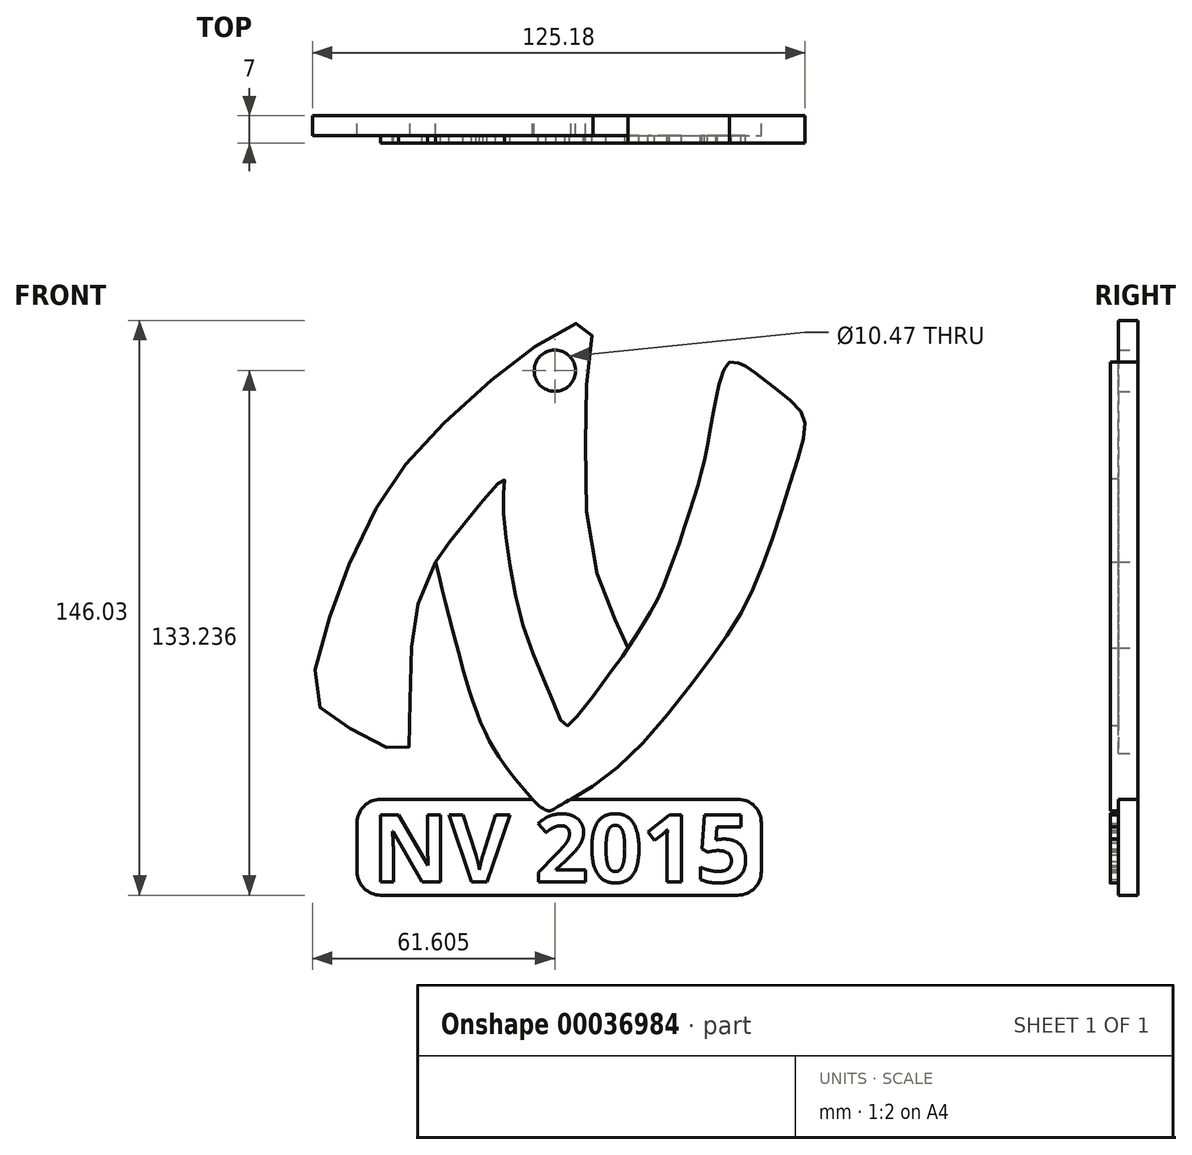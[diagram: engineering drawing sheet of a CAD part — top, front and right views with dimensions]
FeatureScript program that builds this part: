
annotation { "Feature Type Name" : "Feature", "Feature Type Description" : "" }
export const myFeature = defineFeature(function(context is Context, id is Id, definition is map)
    precondition{}
    {
        {
            var Q0;
            Q0=qCreatedBy(makeId("Front.planeOp"),FACE);
            var sketch = newSketch(context, id + "F0", { "sketchPlane" : qUnion([Q0])});
            skFitSpline(sketch, "E0", {"points": [v(-62.05, 9.72) * mm, v(-68.35, 7.94) * mm, v(-78.4, 1.78) * mm, v(-91.86, -9.18) * mm, v(-106.01, -23.1) * mm, v(-113.77, -33.15) * mm, v(-122.67, -50.27) * mm, v(-128.38, -65.56) * mm, v(-132.3, -79.85) * mm, v(-131.8, -87.25) * mm, v(-125.41, -92.27) * mm, v(-121.53, -94.78) * mm, v(-112.63, -99.12) * mm, v(-108.98, -100) * mm, v(-108.07, -97.06) * mm, v(-107.96, -84.07) * mm, v(-107.38, -70.36) * mm, v(-105.68, -61.25) * mm, v(-101.45, -51.4) * mm, v(-90.49, -37.26) * mm, v(-84.1, -30.4) * mm, v(-84.1, -33.38) * mm, v(-83.41, -46.84) * mm, v(-78.16, -70.81) * mm, v(-71.09, -88.16) * mm, v(-68.35, -93.18) * mm, v(-65.32, -90.4) * mm, v(-62.57, -87.07) * mm, v(-59.09, -82.37) * mm, v(-54.2, -75.83) * mm, v(-52.6, -73.32) * mm, v(-53.97, -70.36) * mm, v(-57.16, -62.82) * mm, v(-61.95, -48.67) * mm, v(-63.32, -25.61) * mm, v(-63.1, -7.12) * mm, v(-61.73, 5.66) * mm, v(-62.05, 9.72) * mm]});
            skFitSpline(sketch, "E1", {"points": [v(-26.83, -0.71) * mm, v(-24.57, -0.87) * mm, v(-23.23, -1.48) * mm, v(-21.78, -2.33) * mm, v(-13.33, -8.72) * mm, v(-8.31, -13.74) * mm, v(-7.63, -17.62) * mm, v(-10.3, -28) * mm, v(-16.53, -47.3) * mm, v(-23.38, -63.5) * mm, v(-35.48, -81.31) * mm, v(-57.16, -105.28) * mm, v(-70.17, -113.5) * mm, v(-73.14, -114.64) * mm, v(-78.85, -109.39) * mm, v(-87.06, -98.2) * mm, v(-93.91, -80.63) * mm, v(-101.45, -51.4) * mm], "startDerivative": vector(159.33, 23.9) * mm, "endDerivative": vector(-75.11, 309.54) * mm});
            skFitSpline(sketch, "E2", {"points": [v(-26.83, -0.71) * mm, v(-28.28, -2.88) * mm, v(-28.65, -3.89) * mm, v(-30, -8.72) * mm, v(-33.03, -25.05) * mm, v(-35.79, -35.14) * mm, v(-40.73, -50.04) * mm, v(-45.98, -62.6) * mm, v(-52.6, -73.32) * mm], "startDerivative": vector(-34.78, -41.95) * mm, "endDerivative": vector(-42.22, -64.49) * mm});
            skLineSegment(sketch, "E3.bottom", {"start": v(-121.4, -111.75) * mm, "end": v(-76.8, -111.75) * mm});
            skLineSegment(sketch, "E3.top", {"start": v(-121.4, -136.12) * mm, "end": v(-18.69, -136.12) * mm});
            skLineSegment(sketch, "E3.left", {"start": v(-121.4, -111.75) * mm, "end": v(-121.4, -136.12) * mm});
            skLineSegment(sketch, "E3.right", {"start": v(-18.69, -111.75) * mm, "end": v(-18.69, -136.12) * mm});
            skCircle(sketch, "E4", {"center": v(-71.16, -2.88) * mm, "radius": 5.23 * mm});
            skLineSegment(sketch, "E5.trimOffspring", {"start": v(-67.1, -111.75) * mm, "end": v(-18.69, -111.75) * mm});
            skSolve(sketch);
        }
        {
            var Q0;
            Q0=qCreatedBy(makeId("Front.planeOp"),FACE);
            var sketch = newSketch(context, id + "F1", { "sketchPlane" : qUnion([Q0])});
            skText(sketch, "E6", { "text": "NV 2015", "fontName": "OpenSans-Bold.ttf"});
            const initialGuessF1  = {"E6": [-0.11756, -0.1328, 1, 0, 0.01725]};
            skSetInitialGuess(sketch, initialGuessF1);
            skSolve(sketch);
        }
        {
            var Q0;
            {var subQ1=sQuery(id+"F0.wireOp",EDGE,"E1");Q0=makeQuery(id+"F0.imprint","IMPRINT",FACE,{"disambiguationData":[TD([[makeQuery(id+"F0.imprint","IMPRINT",EDGE,{"derivedFrom":subQ1}),-1.0]])]});}
            extrude(context, id + "F2", {"entities" : qUnion([Q0]), "depth" : 7 * mm});
        }
        {
            var Q0;
            {var subQ0=sQuery(id+"F0.wireOp",EDGE,"E0");var subQ2=makeQuery(id+"F0.imprint","INTERSECT",VERTEX,{"derivedFrom":[subQ0,sQuery(id+"F0.wireOp",EDGE,"E1")]});Q0=makeQuery(id+"F0.imprint","IMPRINT",FACE,{"disambiguationData":[TD([[makeQuery(id+"F0.imprint","IMPRINT",EDGE,{"disambiguationData":[TD([[subQ2,-1.0]])],"derivedFrom":subQ0}),1.0]])]});}
            extrude(context, id + "F3", {"entities" : qUnion([Q0]), "operationType" : NewBodyOperationType.ADD, "depth" : 5 * mm});
        }
        {
            var Q0;
            {var subQ1=sQuery(id+"F0.wireOp",EDGE,"E3.bottom");Q0=makeQuery(id+"F0.imprint","IMPRINT",FACE,{"disambiguationData":[TD([[makeQuery(id+"F0.imprint","IMPRINT",EDGE,{"derivedFrom":subQ1}),-1.0]])]});}
            extrude(context, id + "F4", {"entities" : qUnion([Q0]), "operationType" : NewBodyOperationType.ADD, "depth" : 5 * mm});
        }
        {
            var Q0;
            Q0=makeQuery(id+"F4.opExtrude","SWEPT_EDGE",EDGE,{"disambiguationData":[OSD([sQuery(id+"F0.wireOp",EDGE,"E3.right"),sQuery(id+"F0.wireOp",EDGE,"E5.trimOffspring")])]});
            var Q1;
            Q1=makeQuery(id+"F4.opExtrude","SWEPT_EDGE",EDGE,{"disambiguationData":[OSD([sQuery(id+"F0.wireOp",EDGE,"E3.top"),sQuery(id+"F0.wireOp",EDGE,"E3.right")])]});
            var Q2;
            Q2=makeQuery(id+"F4.opExtrude","SWEPT_EDGE",EDGE,{"disambiguationData":[OSD([sQuery(id+"F0.wireOp",EDGE,"E3.top"),sQuery(id+"F0.wireOp",EDGE,"E3.left")])]});
            var Q3;
            Q3=makeQuery(id+"F4.opExtrude","SWEPT_EDGE",EDGE,{"disambiguationData":[OSD([sQuery(id+"F0.wireOp",EDGE,"E3.bottom"),sQuery(id+"F0.wireOp",EDGE,"E3.left")])]});
            fillet(context, id + "F5", {"entities" : qUnion([Q0, Q1, Q2, Q3]), "radius" : 6 * mm, "tangentPropagation" : true, "allowEdgeOverflow" : false});
        }
        {
            var Q0;
            Q0 = qSketchRegion(id + "F1", true);
            extrude(context, id + "F6", {"entities" : qUnion([Q0]), "operationType" : NewBodyOperationType.ADD, "depth" : 7 * mm});
        }
    });
